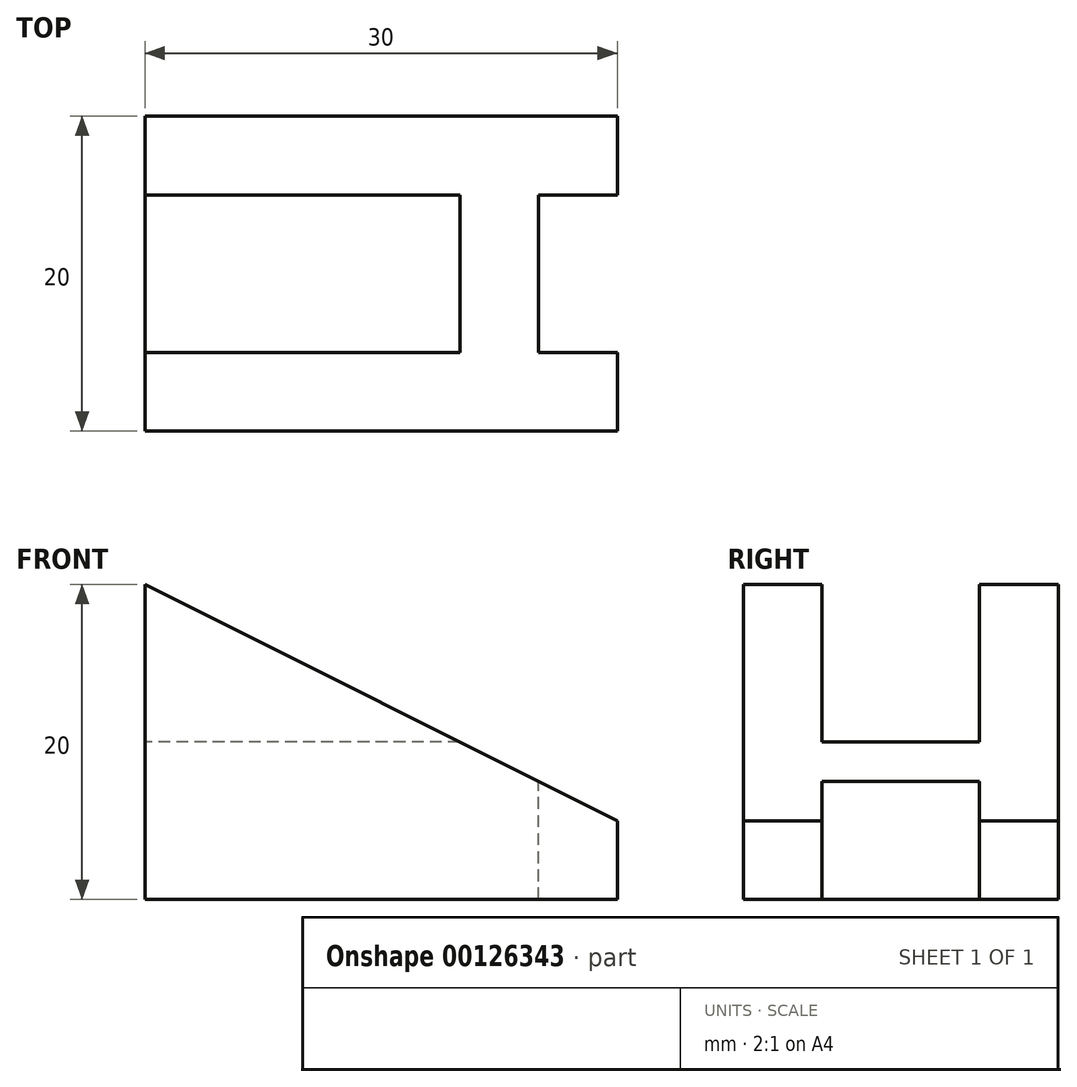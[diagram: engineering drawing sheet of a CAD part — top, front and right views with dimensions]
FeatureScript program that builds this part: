
annotation { "Feature Type Name" : "Feature", "Feature Type Description" : "" }
export const myFeature = defineFeature(function(context is Context, id is Id, definition is map)
    precondition{}
    {
        {
            var Q0;
            Q0=qCreatedBy(makeId("Front.planeOp"),FACE);
            var sketch = newSketch(context, id + "F0", { "sketchPlane" : qUnion([Q0])});
            skLineSegment(sketch, "E0", {"start": v(0, 0) * mm, "end": v(0, 20) * mm});
            skLineSegment(sketch, "E1", {"start": v(0, 20) * mm, "end": v(30, 5) * mm});
            skLineSegment(sketch, "E2", {"start": v(30, 5) * mm, "end": v(30, 0) * mm});
            skLineSegment(sketch, "E3", {"start": v(30, 0) * mm, "end": v(0, 0) * mm});
            skSolve(sketch);
        }
        {
            var Q0;
            Q0=makeQuery(id+"F0.imprint","IMPRINT",FACE,{"disambiguationData":[TD([[makeQuery(id+"F0.imprint","IMPRINT",EDGE,{"derivedFrom":sQuery(id+"F0.wireOp",EDGE,"E0")}),-1.0]])]});
            extrude(context, id + "F1", {"entities" : qUnion([Q0]), "oppositeDirection" : true, "depth" : 20 * mm});
        }
        {
            var Q0;
            Q0=makeQuery(id+"F1.opExtrude","SWEPT_FACE",FACE,{"disambiguationData":[OSD([sQuery(id+"F0.wireOp",EDGE,"E2")])]});
            var sketch = newSketch(context, id + "F2", { "sketchPlane" : qUnion([Q0])});
            skLineSegment(sketch, "E4", {"start": v(15, 0) * mm, "end": v(5, 0) * mm});
            skLineSegment(sketch, "E5", {"start": v(5, 0) * mm, "end": v(5, 7.5) * mm});
            skLineSegment(sketch, "E6", {"start": v(5, 7.5) * mm, "end": v(15, 7.5) * mm});
            skLineSegment(sketch, "E7", {"start": v(15, 7.5) * mm, "end": v(15, 0) * mm});
            skSolve(sketch);
        }
        {
            var Q0;
            {var subQ0=sQuery(id+"F2.wireOp",EDGE,"E6");Q0=makeQuery(id+"F2.imprint","IMPRINT",FACE,{"disambiguationData":[TD([[makeQuery(id+"F2.imprint","IMPRINT",EDGE,{"derivedFrom":subQ0}),-1.0]])]});}
            var Q1;
            {var subQ0=sQuery(id+"F2.wireOp",EDGE,"E4");Q1=makeQuery(id+"F2.imprint","IMPRINT",FACE,{"disambiguationData":[TD([[makeQuery(id+"F2.imprint","IMPRINT",EDGE,{"derivedFrom":subQ0}),-1.0]])]});}
            extrude(context, id + "F3", {"entities" : qUnion([Q0, Q1]), "operationType" : NewBodyOperationType.REMOVE, "oppositeDirection" : true, "depth" : 5 * mm});
        }
        {
            var Q0;
            Q0=makeQuery(id+"F1.opExtrude","SWEPT_FACE",FACE,{"disambiguationData":[OSD([sQuery(id+"F0.wireOp",EDGE,"E0")])]});
            var sketch = newSketch(context, id + "F4", { "sketchPlane" : qUnion([Q0])});
            skLineSegment(sketch, "E8", {"start": v(-15, 20) * mm, "end": v(-15, 10) * mm});
            skLineSegment(sketch, "E9", {"start": v(-15, 10) * mm, "end": v(-5, 10) * mm});
            skLineSegment(sketch, "E10", {"start": v(-5, 10) * mm, "end": v(-5, 20) * mm});
            skLineSegment(sketch, "E11", {"start": v(-5, 20) * mm, "end": v(-15, 20) * mm});
            skSolve(sketch);
        }
        {
            var Q0;
            Q0=makeQuery(id+"F4.imprint","IMPRINT",FACE,{"disambiguationData":[TD([[makeQuery(id+"F4.imprint","IMPRINT",EDGE,{"derivedFrom":sQuery(id+"F4.wireOp",EDGE,"E8")}),1.0]])]});
            extrude(context, id + "F5", {"entities" : qUnion([Q0]), "operationType" : NewBodyOperationType.REMOVE, "endBound" : BoundingType.THROUGH_ALL, "oppositeDirection" : true, "depth" : 25 * mm});
        }
    });
